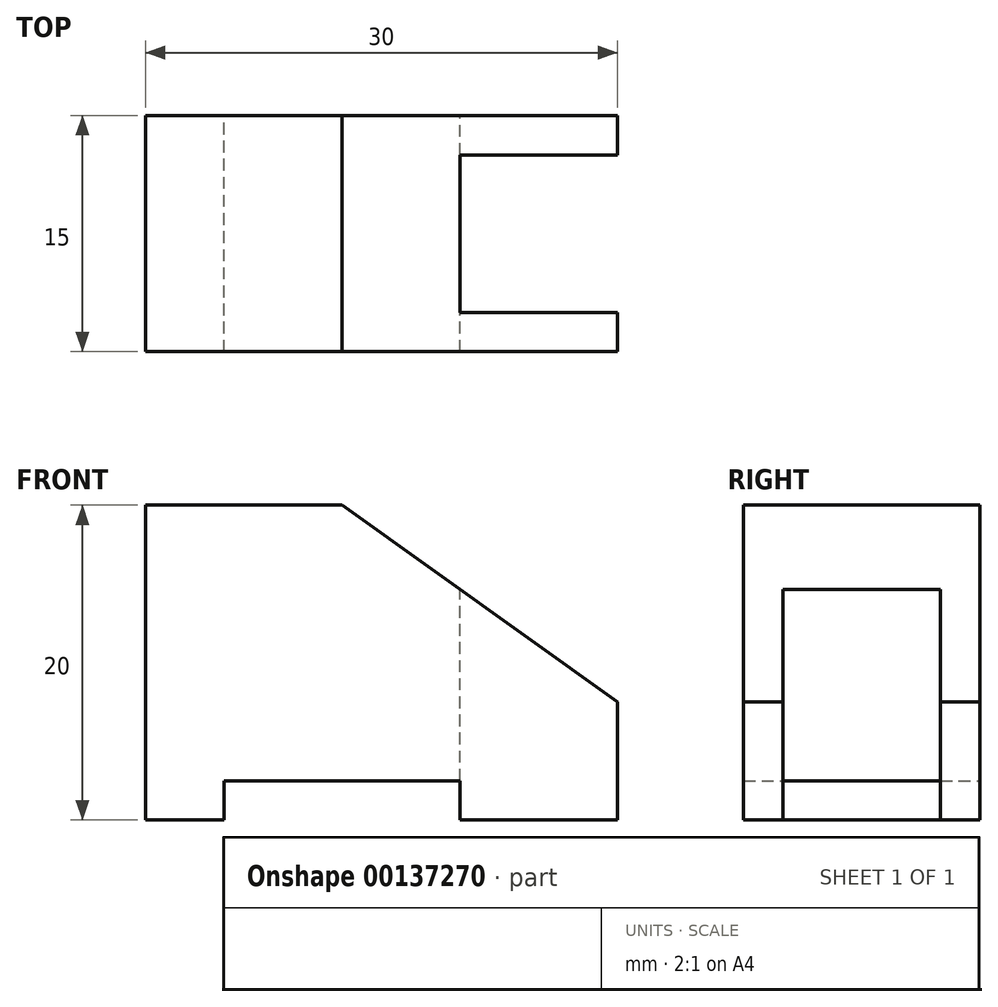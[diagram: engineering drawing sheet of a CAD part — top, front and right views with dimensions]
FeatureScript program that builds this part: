
annotation { "Feature Type Name" : "Feature", "Feature Type Description" : "" }
export const myFeature = defineFeature(function(context is Context, id is Id, definition is map)
    precondition{}
    {
        {
            var Q0;
            Q0=qCreatedBy(makeId("Front.planeOp"),FACE);
            var sketch = newSketch(context, id + "F0", { "sketchPlane" : qUnion([Q0])});
            skLineSegment(sketch, "E0", {"start": v(0, 0) * mm, "end": v(0, 20) * mm});
            skLineSegment(sketch, "E1", {"start": v(0, 20) * mm, "end": v(12.5, 20) * mm});
            skLineSegment(sketch, "E2", {"start": v(12.5, 20) * mm, "end": v(30, 7.5) * mm});
            skLineSegment(sketch, "E3", {"start": v(0, 0) * mm, "end": v(5, 0) * mm});
            skLineSegment(sketch, "E4", {"start": v(5, 0) * mm, "end": v(5, 2.5) * mm});
            skLineSegment(sketch, "E5", {"start": v(5, 2.5) * mm, "end": v(20, 2.5) * mm});
            skLineSegment(sketch, "E6", {"start": v(20, 2.5) * mm, "end": v(20, 0) * mm});
            skLineSegment(sketch, "E7", {"start": v(20, 0) * mm, "end": v(30, 0) * mm});
            skLineSegment(sketch, "E8", {"start": v(30, 7.5) * mm, "end": v(30, 0) * mm});
            skSolve(sketch);
        }
        {
            var Q0;
            Q0=makeQuery(id+"F0.imprint","IMPRINT",FACE,{"disambiguationData":[TD([[makeQuery(id+"F0.imprint","IMPRINT",EDGE,{"derivedFrom":sQuery(id+"F0.wireOp",EDGE,"E0")}),-1.0]])]});
            extrude(context, id + "F1", {"entities" : qUnion([Q0]), "endBound" : BoundingType.SYMMETRIC, "depth" : 15 * mm});
        }
        {
            var Q0;
            Q0=makeQuery(id+"F1.opExtrude","SWEPT_FACE",FACE,{"disambiguationData":[OSD([sQuery(id+"F0.wireOp",EDGE,"E1")])]});
            var sketch = newSketch(context, id + "F2", { "sketchPlane" : qUnion([Q0])});
            skLineSegment(sketch, "E9.0", {"start": v(30, -7.5) * mm, "end": v(30, 7.5) * mm});
            skLineSegment(sketch, "E10", {"start": v(30, 5) * mm, "end": v(20, 5) * mm});
            skLineSegment(sketch, "E11", {"start": v(20, 5) * mm, "end": v(20, -5) * mm});
            skLineSegment(sketch, "E12", {"start": v(20, -5) * mm, "end": v(30, -5) * mm});
            skSolve(sketch);
        }
        {
            var Q0;
            {var subQ0=sQuery(id+"F2.wireOp",EDGE,"E10");Q0=makeQuery(id+"F2.imprint","IMPRINT",FACE,{"disambiguationData":[TD([[makeQuery(id+"F2.imprint","IMPRINT",EDGE,{"derivedFrom":subQ0}),1.0]])]});}
            extrude(context, id + "F3", {"entities" : qUnion([Q0]), "operationType" : NewBodyOperationType.REMOVE, "endBound" : BoundingType.THROUGH_ALL, "oppositeDirection" : true, "depth" : 25 * mm});
        }
    });
